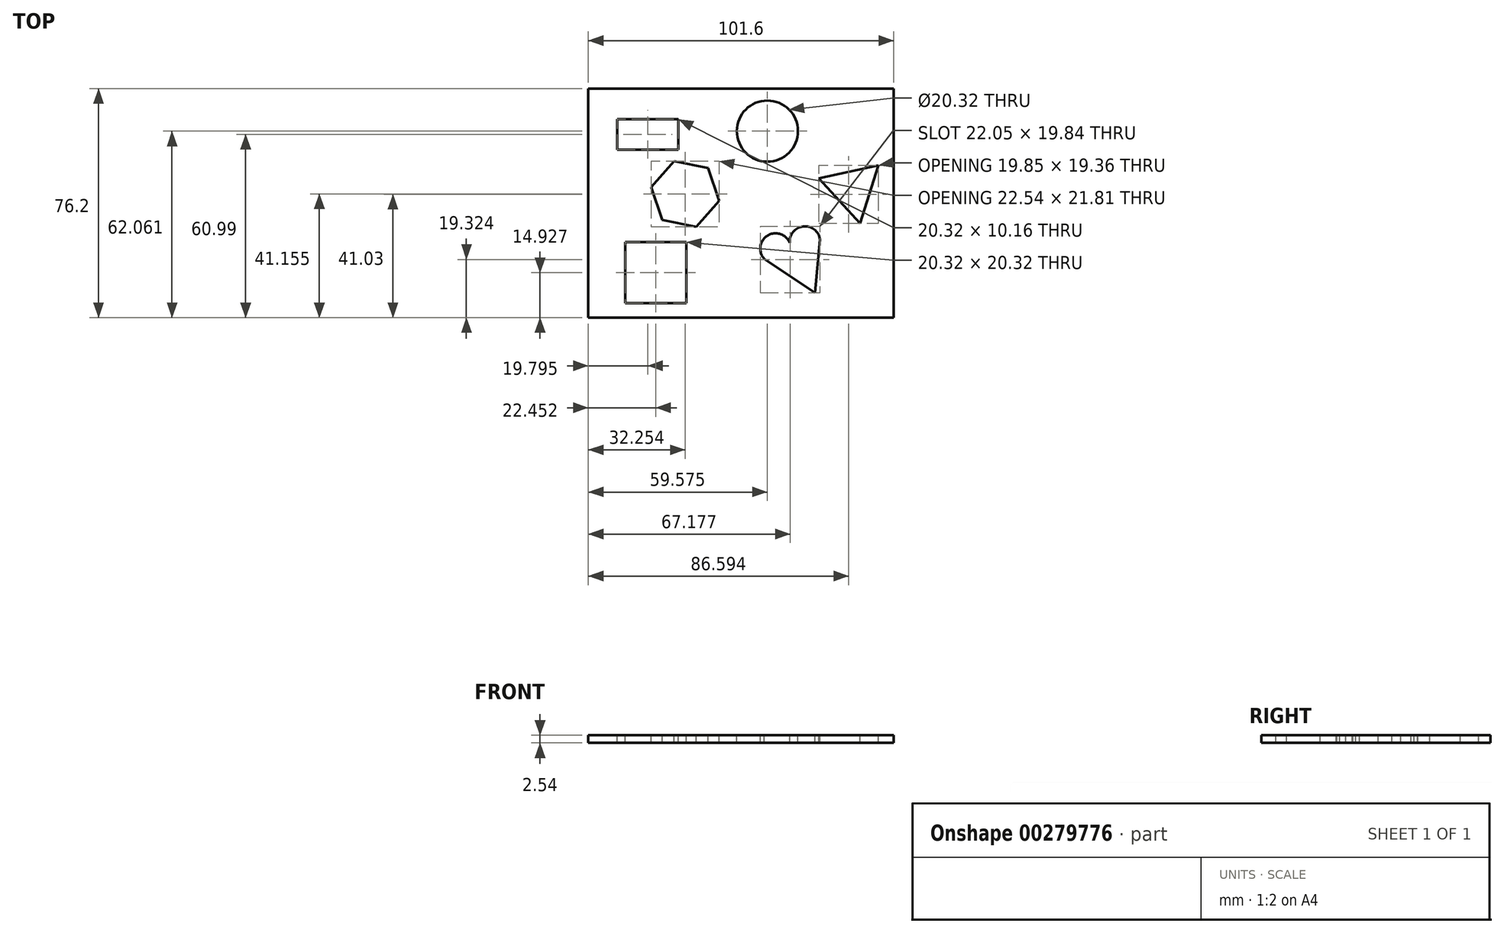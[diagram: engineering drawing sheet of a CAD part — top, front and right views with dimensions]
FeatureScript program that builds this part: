
annotation { "Feature Type Name" : "Feature", "Feature Type Description" : "" }
export const myFeature = defineFeature(function(context is Context, id is Id, definition is map)
    precondition{}
    {
        {
            var Q0;
            Q0=qCreatedBy(makeId("Top.planeOp"),FACE);
            var sketch = newSketch(context, id + "F0", { "sketchPlane" : qUnion([Q0])});
            skLineSegment(sketch, "E0.bottom", {"start": v(2.49, 0) * mm, "end": v(104.09, 0) * mm});
            skLineSegment(sketch, "E0.top", {"start": v(2.49, 76.2) * mm, "end": v(104.09, 76.2) * mm});
            skLineSegment(sketch, "E0.left", {"start": v(2.49, 0) * mm, "end": v(2.49, 76.2) * mm});
            skLineSegment(sketch, "E0.right", {"start": v(104.09, 0) * mm, "end": v(104.09, 76.2) * mm});
            skSolve(sketch);
        }
        {
            var Q0;
            Q0 = qSketchRegion(id + "F0", true);
            extrude(context, id + "F1", {"entities" : qUnion([Q0]), "depth" : 2.54 * mm});
        }
        {
            var Q0;
            Q0=makeQuery(id+"F1.opExtrude","CAP_FACE",FACE,{"disambiguationData":[OSD([sQuery(id+"F0.wireOp",EDGE,"E0.bottom"),sQuery(id+"F0.wireOp",EDGE,"E0.top"),sQuery(id+"F0.wireOp",EDGE,"E0.left"),sQuery(id+"F0.wireOp",EDGE,"E0.right")])],"isStart":false});
            var sketch = newSketch(context, id + "F2", { "sketchPlane" : qUnion([Q0])});
            skCircle(sketch, "E1.cCircle", {"center": v(34.74, 41.15) * mm, "radius": 9.96 * mm, "construction": true});
            skLineSegment(sketch, "E1.0", {"start": v(42.37, 49.77) * mm, "end": v(46.01, 38.86) * mm});
            skLineSegment(sketch, "E1.1", {"start": v(46.01, 38.86) * mm, "end": v(38.39, 30.25) * mm});
            skLineSegment(sketch, "E1.2", {"start": v(38.39, 30.25) * mm, "end": v(27.12, 32.54) * mm});
            skLineSegment(sketch, "E1.3", {"start": v(27.12, 32.54) * mm, "end": v(23.48, 43.45) * mm});
            skLineSegment(sketch, "E1.4", {"start": v(23.48, 43.45) * mm, "end": v(31.1, 52.06) * mm});
            skLineSegment(sketch, "E1.5", {"start": v(31.1, 52.06) * mm, "end": v(42.37, 49.77) * mm});
            skPoint(sketch, "E1.0.midPoint", {"position": v(44.2, 44.31) * mm});
            skCircle(sketch, "E2", {"center": v(62.07, 62.06) * mm, "radius": 10.16 * mm});
            skLineSegment(sketch, "E3.bottom", {"start": v(14.78, 4.77) * mm, "end": v(35.1, 4.77) * mm});
            skLineSegment(sketch, "E3.top", {"start": v(14.78, 25.09) * mm, "end": v(35.1, 25.09) * mm});
            skLineSegment(sketch, "E3.left", {"start": v(14.78, 4.77) * mm, "end": v(14.78, 25.09) * mm});
            skLineSegment(sketch, "E3.right", {"start": v(35.1, 4.77) * mm, "end": v(35.1, 25.09) * mm});
            skLineSegment(sketch, "E4", {"start": v(61, 19.57) * mm, "end": v(77.91, 8.3) * mm});
            skLineSegment(sketch, "E5", {"start": v(77.91, 8.3) * mm, "end": v(79.59, 26.04) * mm});
            skLineSegment(sketch, "E6", {"start": v(79.16, 46.37) * mm, "end": v(92.85, 31.35) * mm});
            skLineSegment(sketch, "E7", {"start": v(92.85, 31.35) * mm, "end": v(99, 50.71) * mm});
            skLineSegment(sketch, "E8", {"start": v(99, 50.71) * mm, "end": v(79.16, 46.37) * mm});
            skArc(sketch, "E9", {"start": v(79.59, 26.04) * mm, "mid": v(73.26, 30.22) * mm, "end": v(69.83, 23.45) * mm});
            skArc(sketch, "E10", {"start": v(69.83, 23.45) * mm, "mid": v(62.73, 27.62) * mm, "end": v(61, 19.57) * mm});
            skLineSegment(sketch, "E11.bottom", {"start": v(12.13, 66.07) * mm, "end": v(32.45, 66.07) * mm});
            skLineSegment(sketch, "E11.top", {"start": v(12.13, 55.91) * mm, "end": v(32.45, 55.91) * mm});
            skLineSegment(sketch, "E11.left", {"start": v(12.13, 66.07) * mm, "end": v(12.13, 55.91) * mm});
            skLineSegment(sketch, "E11.right", {"start": v(32.45, 66.07) * mm, "end": v(32.45, 55.91) * mm});
            skSolve(sketch);
        }
        {
            var Q0;
            Q0 = qSketchRegion(id + "F2", true);
            extrude(context, id + "F3", {"entities" : qUnion([Q0]), "operationType" : NewBodyOperationType.REMOVE, "oppositeDirection" : true, "depth" : 25.4 * mm});
        }
    });
